# Revit family: 1
name_source: partatom
category: Pipe Accessories
revit_build: Autodesk Revit 2018 (Build: 20190510_1515(x64)
units: mm (PartAtom-declared; Revit-internal decimal feet)

## family parameters
Always vertical = No
Cut with Voids When Loaded = No
OmniClass Number = 23.65.00.00
OmniClass Title = Supply and Distribution of Liquids and Gases
Part Type = Normal
Round Connector Dimension = Use Diameter
Shared = No
Work Plane-Based = No

## types (1)
- 554 - 3/4” - Female differential by-pass valve with pipe union
    A = 64 mm  [stored 0.209974 ft]
    Antifreeze: = Passiveted Propylene Glycol
    Application fluids = Water or glycol solutions
    B = 22 mm  [stored 0.0721785 ft]
    BIMobject category = HVAC: Other HVAC
    Body Material = Pintossi - Metal - Brass CW617N
    Brand url = http://www.pintossi.it
    C = 90 mm
    CH = 38 mm  [stored 0.124672 ft]
    Conditioning: = as indicated by the producer
    Copper (CU): = < 0,1 mg/kg (< 0,05 mg/kg for steam)
    D = 112 mm
    Description = Pintossi+C differential by-pass valve is the perfect solutions in order to avoid noise in heating systems using two ways motorized zone valves or thermostatic radiator valves.

The valve limits the maximum differential pressure value when the pump is in function, ensuring a flow recirculation proportional to the simultaneous number of valves closed.
    Design country = Italy
    Edition number = 1
    Fluid aspect: = Limpid
    Gaskets Material = Pintossi - Rubber - NBR
    IFC Classification = Valve
    Iron (FE): = < 0,5 mg/kg (< 0,1 mg/kg for steam)
    Main Inlet/Outlet Diameter = 19 mm
    Manufacturer = Pintossi+c
    Manufacturer country = Italy
    Manufacturer name = Pintossi+c
    Masterformat 2014 Code = 23 05 93
    Masterformat 2014 Description = Testing, Adjusting, and Balancing for HVAC
    Material main = Brass
    Maximum percentage of glycol [%] = 30
    Maximum working pressure = 1000000.0 Pa
    Maximum working temperature = 100 °C
    Model = 554
    NBS Reference Code = 35-83-06
    NBS Reference Description = Balancing Equipment
    Obturator Material = Pintossi - Metal - Brass CW617N
    PH: = Between 7 and 8
    Product Guid = a1516ca7-c29a-432c-935f-a9d5edb142eb
    Product data url = https://www.bimobject.com
    Product family = Components for central heating systems
    Product group = By-pass-valves
    UNSPSC Code = 401416
    URL = www.pintossi.it
    Uniclass 1.4 Code = L7136
    Uniclass 1.4 Description = Valves
    Uniclass 2.0 Code = PR-35-83-06
    Uniclass 2.0 Description = Balancing Equipment
    Uniclass 2015 Code = Pr_40_50_83_06
    Uniclass 2015 Name = Balancing equipment
    Uniformat II Code = D3070
    Uniformat II Description = Systems Testing & Balancing
    Wheelhandle Material = Pintossi - Plastic - ABS

note: [stored X ft] marks values corroborated as IEEE doubles in the binary element streams (Revit-internal decimal feet)

## geometry (parser evidence)
native form markers: Sweep x2
no freeform markers — native parametric forms only
